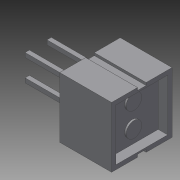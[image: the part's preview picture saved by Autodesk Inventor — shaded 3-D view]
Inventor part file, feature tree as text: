
AUTODESK INVENTOR PART (.ipt)
format: ipt  version: 2014 (Build 180170000, 170)  size: 143,872 bytes
history: native  units: mm
features: extrude x4, sketch x4
ambient origin geometry x8: Origin, YZ Plane, XZ Plane, XY Plane, X Axis, Y Axis, Z Axis, Center Point
bodies: Volumenkörper1 (feature_tree)
feature tree (8):
  extrude  "Extrusion1"  Depth=7.0mm
  extrude  "Extrusion2"  Depth=0.3mm
  extrude  "Extrusion3"  Depth=6.0mm TaperAngle=0.0deg
  extrude  "Extrusion4"  Depth=0.5mm
  sketch  "Skizze1"  dims[d0=7.0mm d1=7.0mm]
  sketch  "Skizze2"  dims[d2=1.0mm d3=0.3mm]
  sketch  "Skizze3"  dims[d5=3.0mm d6=6.0mm d7=0.0mm]
  sketch  "Skizze4"  dims[d8=0.5mm d9=0.5mm d10=0.5mm d11=0.5mm d12=1.1mm d13=0.0mm d14=0.5mm d15=0.5mm d16=0.5mm d17=0.5mm d18=0.5mm d19=0.5mm d20=0.5mm d21=0.5mm d24=1.98mm d25=3.04mm d26=3.04mm d27=1.98mm d28=6.0mm d29=0.0mm d30=1.8mm d31=1.8mm d32=2.8mm d33=3.0mm d34=1.6mm d35=0.2mm d36=0.0mm]
